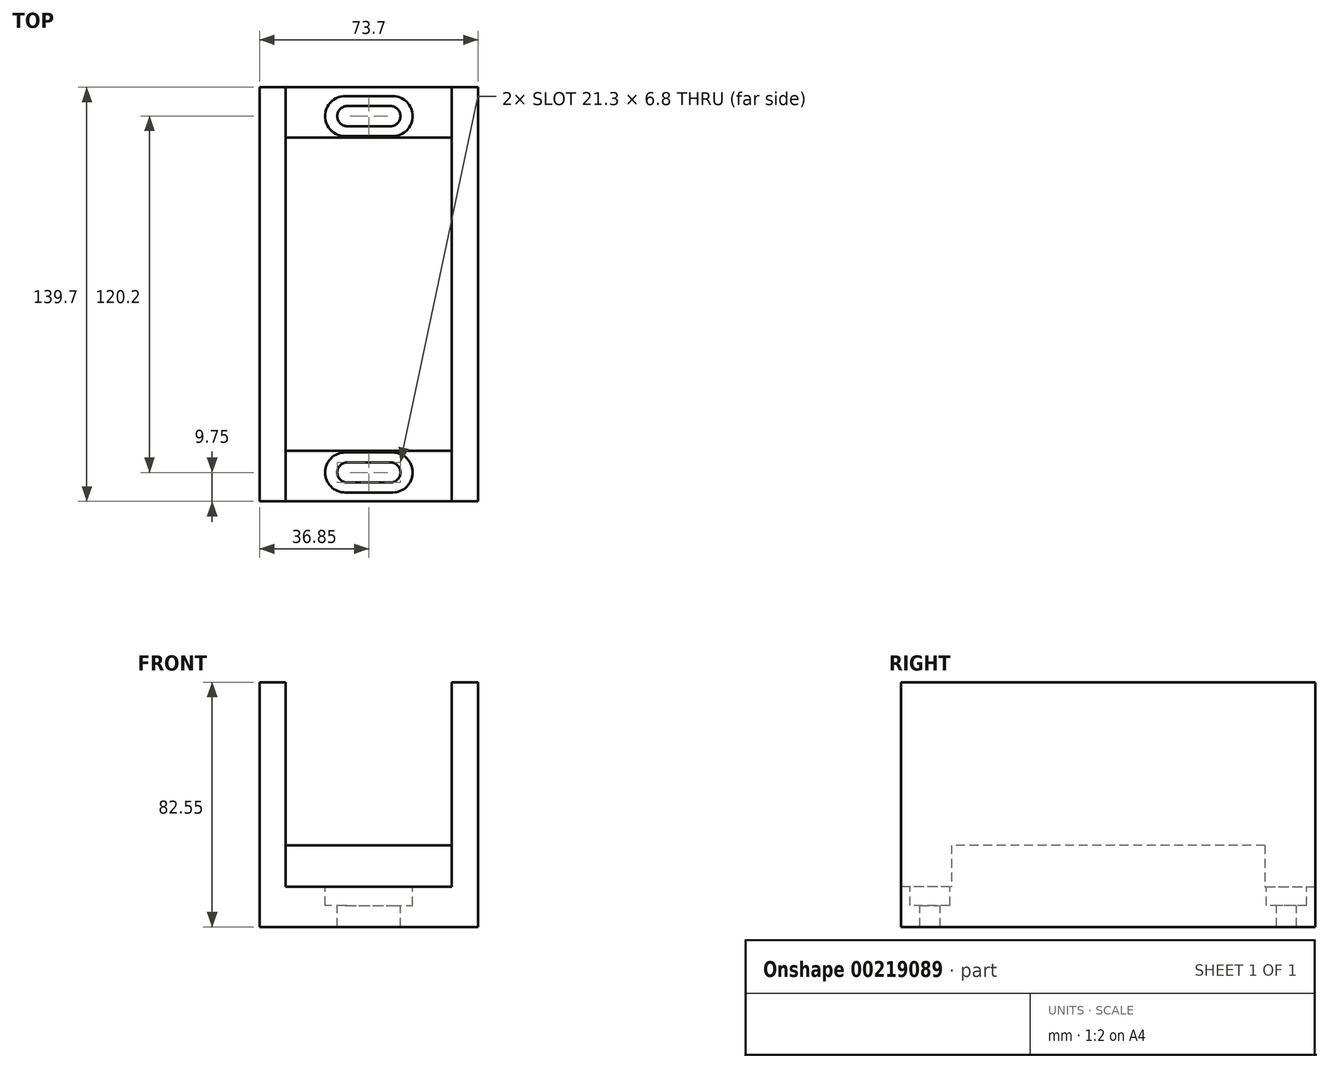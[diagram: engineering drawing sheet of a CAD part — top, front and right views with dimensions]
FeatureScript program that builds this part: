
annotation { "Feature Type Name" : "Feature", "Feature Type Description" : "" }
export const myFeature = defineFeature(function(context is Context, id is Id, definition is map)
    precondition{}
    {
        {
            var Q0;
            Q0=qCreatedBy(makeId("Top.planeOp"),FACE);
            var sketch = newSketch(context, id + "F0", { "sketchPlane" : qUnion([Q0])});
            skLineSegment(sketch, "E0.bottom", {"start": v(0, 0) * mm, "end": v(73.7, 0) * mm});
            skLineSegment(sketch, "E0.top", {"start": v(0, 139.7) * mm, "end": v(73.7, 139.7) * mm});
            skLineSegment(sketch, "E0.left", {"start": v(0, 0) * mm, "end": v(0, 139.7) * mm});
            skLineSegment(sketch, "E0.right", {"start": v(73.7, 0) * mm, "end": v(73.7, 139.7) * mm});
            skSolve(sketch);
        }
        {
            var Q0;
            Q0 = qSketchRegion(id + "F0", true);
            extrude(context, id + "F1", {"entities" : qUnion([Q0]), "depth" : 82.55 * mm});
        }
        {
            var Q0;
            Q0=makeQuery(id+"F1.opExtrude","SWEPT_FACE",FACE,{"disambiguationData":[OSD([sQuery(id+"F0.wireOp",EDGE,"E0.bottom")])]});
            var sketch = newSketch(context, id + "F2", { "sketchPlane" : qUnion([Q0])});
            skLineSegment(sketch, "E1.bottom", {"start": v(8.79, 82.55) * mm, "end": v(64.79, 82.55) * mm});
            skLineSegment(sketch, "E1.top", {"start": v(8.79, 27.55) * mm, "end": v(64.79, 27.55) * mm});
            skLineSegment(sketch, "E1.left", {"start": v(8.79, 82.55) * mm, "end": v(8.79, 27.55) * mm});
            skLineSegment(sketch, "E1.right", {"start": v(64.79, 82.55) * mm, "end": v(64.79, 27.55) * mm});
            skSolve(sketch);
        }
        {
            var Q0;
            Q0 = qSketchRegion(id + "F2", true);
            extrude(context, id + "F3", {"entities" : qUnion([Q0]), "operationType" : NewBodyOperationType.REMOVE, "endBound" : BoundingType.THROUGH_ALL, "oppositeDirection" : true, "depth" : 25 * mm});
        }
        {
            var Q0;
            Q0=makeQuery(id+"F1.opExtrude","SWEPT_FACE",FACE,{"disambiguationData":[OSD([sQuery(id+"F0.wireOp",EDGE,"E0.bottom")])]});
            var sketch = newSketch(context, id + "F4", { "sketchPlane" : qUnion([Q0])});
            skLineSegment(sketch, "E2.bottom", {"start": v(8.79, 27.55) * mm, "end": v(64.79, 27.55) * mm});
            skLineSegment(sketch, "E2.top", {"start": v(8.79, 13.55) * mm, "end": v(64.79, 13.55) * mm});
            skLineSegment(sketch, "E2.left", {"start": v(8.79, 27.55) * mm, "end": v(8.79, 13.55) * mm});
            skLineSegment(sketch, "E2.right", {"start": v(64.79, 27.55) * mm, "end": v(64.79, 13.55) * mm});
            skSolve(sketch);
        }
        {
            var Q0;
            Q0 = qSketchRegion(id + "F4", true);
            extrude(context, id + "F5", {"entities" : qUnion([Q0]), "operationType" : NewBodyOperationType.REMOVE, "oppositeDirection" : true, "depth" : 17 * mm});
        }
        {
            var Q0;
            Q0=makeQuery(id+"F1.opExtrude","SWEPT_FACE",FACE,{"disambiguationData":[OSD([sQuery(id+"F0.wireOp",EDGE,"E0.top")])]});
            var sketch = newSketch(context, id + "F6", { "sketchPlane" : qUnion([Q0])});
            skLineSegment(sketch, "E3.bottom", {"start": v(-64.79, 27.55) * mm, "end": v(-8.79, 27.55) * mm});
            skLineSegment(sketch, "E3.top", {"start": v(-64.79, 13.55) * mm, "end": v(-8.79, 13.55) * mm});
            skLineSegment(sketch, "E3.left", {"start": v(-64.79, 27.55) * mm, "end": v(-64.79, 13.55) * mm});
            skLineSegment(sketch, "E3.right", {"start": v(-8.79, 27.55) * mm, "end": v(-8.79, 13.55) * mm});
            skSolve(sketch);
        }
        {
            var Q0;
            Q0 = qSketchRegion(id + "F6", true);
            extrude(context, id + "F7", {"entities" : qUnion([Q0]), "operationType" : NewBodyOperationType.REMOVE, "oppositeDirection" : true, "depth" : 17 * mm});
        }
        {
            var Q0;
            Q0=makeQuery(id+"F7.boolean.opBoolean","COPY",FACE,{"derivedFrom":makeQuery(id+"F7.opExtrude","SWEPT_FACE",FACE,{"disambiguationData":[OSD([sQuery(id+"F6.wireOp",EDGE,"E3.top")])]})});
            var sketch = newSketch(context, id + "F8", { "sketchPlane" : qUnion([Q0])});
            skLineSegment(sketch, "E4", {"start": v(28.85, 136.7) * mm, "end": v(44.85, 136.7) * mm});
            skLineSegment(sketch, "E5", {"start": v(44.85, 123.2) * mm, "end": v(28.85, 123.2) * mm});
            skArc(sketch, "E6", {"start": v(28.85, 136.7) * mm, "mid": v(22.1, 129.95) * mm, "end": v(28.85, 123.2) * mm});
            skArc(sketch, "E7", {"start": v(44.85, 123.2) * mm, "mid": v(51.6, 129.95) * mm, "end": v(44.85, 136.7) * mm});
            skLineSegment(sketch, "E8", {"start": v(29.6, 133.35) * mm, "end": v(44.1, 133.35) * mm});
            skLineSegment(sketch, "E9", {"start": v(44.1, 126.55) * mm, "end": v(29.6, 126.55) * mm});
            skArc(sketch, "E10", {"start": v(29.6, 133.35) * mm, "mid": v(26.2, 129.95) * mm, "end": v(29.6, 126.55) * mm});
            skArc(sketch, "E11", {"start": v(44.1, 126.55) * mm, "mid": v(47.5, 129.95) * mm, "end": v(44.1, 133.35) * mm});
            skLineSegment(sketch, "E12", {"start": v(14.55, 69.85) * mm, "end": v(59.4, 69.85) * mm});
            skLineSegment(sketch, "E13.MirrorCS", {"start": v(44.1, 13.15) * mm, "end": v(29.6, 13.15) * mm});
            skLineSegment(sketch, "E14.MirrorCS", {"start": v(29.6, 6.35) * mm, "end": v(44.1, 6.35) * mm});
            skArc(sketch, "E15.MirrorCS", {"start": v(44.85, 16.5) * mm, "mid": v(51.6, 9.75) * mm, "end": v(44.85, 3) * mm});
            skArc(sketch, "E16.MirrorCS", {"start": v(44.1, 13.15) * mm, "mid": v(47.5, 9.75) * mm, "end": v(44.1, 6.35) * mm});
            skArc(sketch, "E17.MirrorCS", {"start": v(28.85, 3) * mm, "mid": v(22.1, 9.75) * mm, "end": v(28.85, 16.5) * mm});
            skLineSegment(sketch, "E18.MirrorCS", {"start": v(28.85, 3) * mm, "end": v(44.85, 3) * mm});
            skLineSegment(sketch, "E19.MirrorCS", {"start": v(44.85, 16.5) * mm, "end": v(28.85, 16.5) * mm});
            skArc(sketch, "E20.MirrorCS", {"start": v(29.6, 6.35) * mm, "mid": v(26.2, 9.75) * mm, "end": v(29.6, 13.15) * mm});
            skSolve(sketch);
        }
        {
            var Q0;
            Q0 = qSketchRegion(id + "F8", true);
            extrude(context, id + "F9", {"entities" : qUnion([Q0]), "operationType" : NewBodyOperationType.REMOVE, "oppositeDirection" : true, "depth" : 6.3 * mm});
        }
        {
            var Q0;
            Q0=makeQuery(id+"F9.boolean.opBoolean","SPLIT",FACE,{"disambiguationData":[TD([makeQuery(id+"F9.opExtrude","SWEPT_FACE",FACE,{"disambiguationData":[OSD([sQuery(id+"F8.wireOp",EDGE,"E8")])]})])],"derivedFrom":makeQuery(id+"F7.boolean.opBoolean","COPY",FACE,{"derivedFrom":makeQuery(id+"F7.opExtrude","SWEPT_FACE",FACE,{"disambiguationData":[OSD([sQuery(id+"F6.wireOp",EDGE,"E3.top")])]})})});
            var Q1;
            Q1=makeQuery(id+"F9.boolean.opBoolean","SPLIT",FACE,{"disambiguationData":[TD([makeQuery(id+"F9.opExtrude","SWEPT_FACE",FACE,{"disambiguationData":[OSD([sQuery(id+"F8.wireOp",EDGE,"E13.MirrorCS")])]})])],"derivedFrom":makeQuery(id+"F5.boolean.opBoolean","COPY",FACE,{"derivedFrom":makeQuery(id+"F5.opExtrude","SWEPT_FACE",FACE,{"disambiguationData":[OSD([sQuery(id+"F4.wireOp",EDGE,"E2.top")])]})})});
            extrude(context, id + "F10", {"entities" : qUnion([Q0, Q1]), "operationType" : NewBodyOperationType.REMOVE, "endBound" : BoundingType.THROUGH_ALL, "oppositeDirection" : true, "depth" : 25 * mm});
        }
    });
